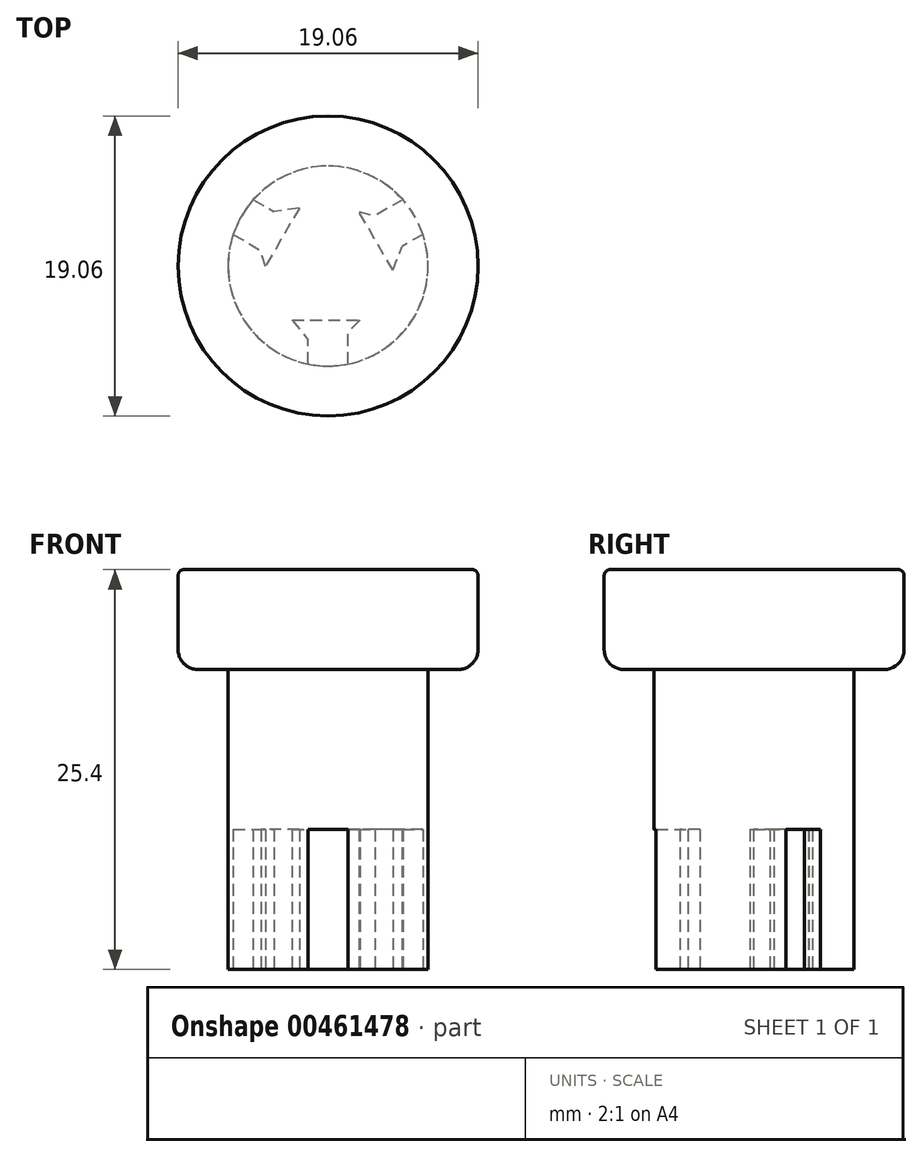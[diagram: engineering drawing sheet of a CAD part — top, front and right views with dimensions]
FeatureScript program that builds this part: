
annotation { "Feature Type Name" : "Feature", "Feature Type Description" : "" }
export const myFeature = defineFeature(function(context is Context, id is Id, definition is map)
    precondition{}
    {
        {
            var Q0;
            Q0=qCreatedBy(makeId("Top.planeOp"),FACE);
            var sketch = newSketch(context, id + "F0", { "sketchPlane" : qUnion([Q0])});
            skCircle(sketch, "E0", {"center": v(0, 0) * mm, "radius": 9.53 * mm});
            skSolve(sketch);
        }
        {
            var Q0;
            Q0=makeQuery(id+"F0.imprint","IMPRINT",FACE,{"disambiguationData":[TD([[makeQuery(id+"F0.imprint","IMPRINT",EDGE,{"derivedFrom":sQuery(id+"F0.wireOp",EDGE,"E0")}),1.0]])]});
            extrude(context, id + "F1", {"entities" : qUnion([Q0]), "depth" : 6.35 * mm});
        }
        {
            var Q0;
            Q0=makeQuery(id+"F1.opExtrude","CAP_FACE",FACE,{"disambiguationData":[OSD([sQuery(id+"F0.wireOp",EDGE,"E0")])],"isStart":true});
            var sketch = newSketch(context, id + "F2", { "sketchPlane" : qUnion([Q0])});
            skCircle(sketch, "E1", {"center": v(0, 0) * mm, "radius": 6.35 * mm});
            skSolve(sketch);
        }
        {
            var Q0;
            Q0=makeQuery(id+"F2.imprint","IMPRINT",FACE,{"disambiguationData":[TD([[makeQuery(id+"F2.imprint","IMPRINT",EDGE,{"derivedFrom":sQuery(id+"F2.wireOp",EDGE,"E1")}),1.0]])]});
            extrude(context, id + "F3", {"entities" : qUnion([Q0]), "operationType" : NewBodyOperationType.ADD, "depth" : 19.05 * mm});
        }
        {
            var Q0;
            Q0=makeQuery(id+"F3.opExtrude","CAP_FACE",FACE,{"disambiguationData":[OSD([sQuery(id+"F2.wireOp",EDGE,"E1")])],"isStart":false});
            var sketch = newSketch(context, id + "F4", { "sketchPlane" : qUnion([Q0])});
            skLineSegment(sketch, "E2", {"start": v(0, 6.35) * mm, "end": v(-1.27, 6.35) * mm});
            skLineSegment(sketch, "E3", {"start": v(-1.27, 6.35) * mm, "end": v(-1.27, 4.7) * mm});
            skLineSegment(sketch, "E4", {"start": v(-2.29, 3.43) * mm, "end": v(-1.27, 4.7) * mm});
            skLineSegment(sketch, "E5", {"start": v(0, 6.35) * mm, "end": v(1.27, 6.35) * mm});
            skLineSegment(sketch, "E6", {"start": v(1.27, 6.35) * mm, "end": v(1.27, 4.2) * mm});
            skLineSegment(sketch, "E7", {"start": v(1.27, 3.43) * mm, "end": v(2.03, 3.43) * mm});
            skLineSegment(sketch, "E8", {"start": v(2.03, 3.43) * mm, "end": v(1.27, 4.2) * mm});
            skLineSegment(sketch, "E9", {"start": v(-2.29, 3.43) * mm, "end": v(2.03, 3.43) * mm});
            skLineSegment(sketch, "E10.1.0", {"start": v(-1.83, -3.7) * mm, "end": v(-3.99, 0.05) * mm});
            skLineSegment(sketch, "E10.1.1", {"start": v(-1.83, -3.7) * mm, "end": v(-3.43, -3.45) * mm});
            skLineSegment(sketch, "E10.1.2", {"start": v(-4.86, -4.27) * mm, "end": v(-3.43, -3.45) * mm});
            skLineSegment(sketch, "E10.1.3", {"start": v(-5.5, -3.17) * mm, "end": v(-4.86, -4.27) * mm});
            skLineSegment(sketch, "E10.1.4", {"start": v(-5.5, -3.17) * mm, "end": v(-6.13, -2.08) * mm});
            skLineSegment(sketch, "E10.1.5", {"start": v(-6.13, -2.08) * mm, "end": v(-4.26, -1) * mm});
            skLineSegment(sketch, "E10.1.6", {"start": v(-3.99, 0.05) * mm, "end": v(-4.26, -1) * mm});
            skLineSegment(sketch, "E10.2.0", {"start": v(4.11, 0.27) * mm, "end": v(1.95, -3.47) * mm});
            skLineSegment(sketch, "E10.2.1", {"start": v(4.11, 0.27) * mm, "end": v(4.7, -1.25) * mm});
            skLineSegment(sketch, "E10.2.2", {"start": v(6.13, -2.08) * mm, "end": v(4.7, -1.25) * mm});
            skLineSegment(sketch, "E10.2.3", {"start": v(5.5, -3.18) * mm, "end": v(6.13, -2.08) * mm});
            skLineSegment(sketch, "E10.2.4", {"start": v(5.5, -3.18) * mm, "end": v(4.86, -4.27) * mm});
            skLineSegment(sketch, "E10.2.5", {"start": v(4.86, -4.27) * mm, "end": v(3, -3.2) * mm});
            skLineSegment(sketch, "E10.2.6", {"start": v(1.95, -3.47) * mm, "end": v(3, -3.2) * mm});
            skPoint(sketch, "E10.center", {"position": v(0, 0) * mm});
            skSolve(sketch);
        }
        {
            var Q0;
            {var subQ7=sQuery(id+"F4.wireOp",EDGE,"E4");Q0=makeQuery(id+"F4.imprint","IMPRINT",FACE,{"disambiguationData":[TD([[makeQuery(id+"F4.imprint","IMPRINT",EDGE,{"derivedFrom":subQ7}),-1.0]])]});}
            var Q1;
            Q1=makeQuery(id+"F4.imprint","IMPRINT",FACE,{"disambiguationData":[TD([[makeQuery(id+"F4.imprint","IMPRINT",EDGE,{"derivedFrom":sQuery(id+"F4.wireOp",EDGE,"E10.1.0")}),1.0]])]});
            var Q2;
            Q2=makeQuery(id+"F4.imprint","IMPRINT",FACE,{"disambiguationData":[TD([[makeQuery(id+"F4.imprint","IMPRINT",EDGE,{"derivedFrom":sQuery(id+"F4.wireOp",EDGE,"E10.2.0")}),1.0]])]});
            extrude(context, id + "F5", {"entities" : qUnion([Q0, Q1, Q2]), "operationType" : NewBodyOperationType.REMOVE, "oppositeDirection" : true, "depth" : 8.9 * mm});
        }
        {
            var Q0;
            Q0=makeQuery(id+"F1.opExtrude","CAP_EDGE",EDGE,{"disambiguationData":[OSD([sQuery(id+"F0.wireOp",EDGE,"E0")])],"isStart":true});
            fillet(context, id + "F6", {"entities" : qUnion([Q0]), "radius" : 1.27 * mm, "tangentPropagation" : true, "allowEdgeOverflow" : false});
        }
        {
            var Q0;
            Q0=makeQuery(id+"F1.opExtrude","CAP_EDGE",EDGE,{"disambiguationData":[OSD([sQuery(id+"F0.wireOp",EDGE,"E0")])],"isStart":false});
            fillet(context, id + "F7", {"entities" : qUnion([Q0]), "radius" : 0.38 * mm, "tangentPropagation" : true, "allowEdgeOverflow" : false});
        }
    });
